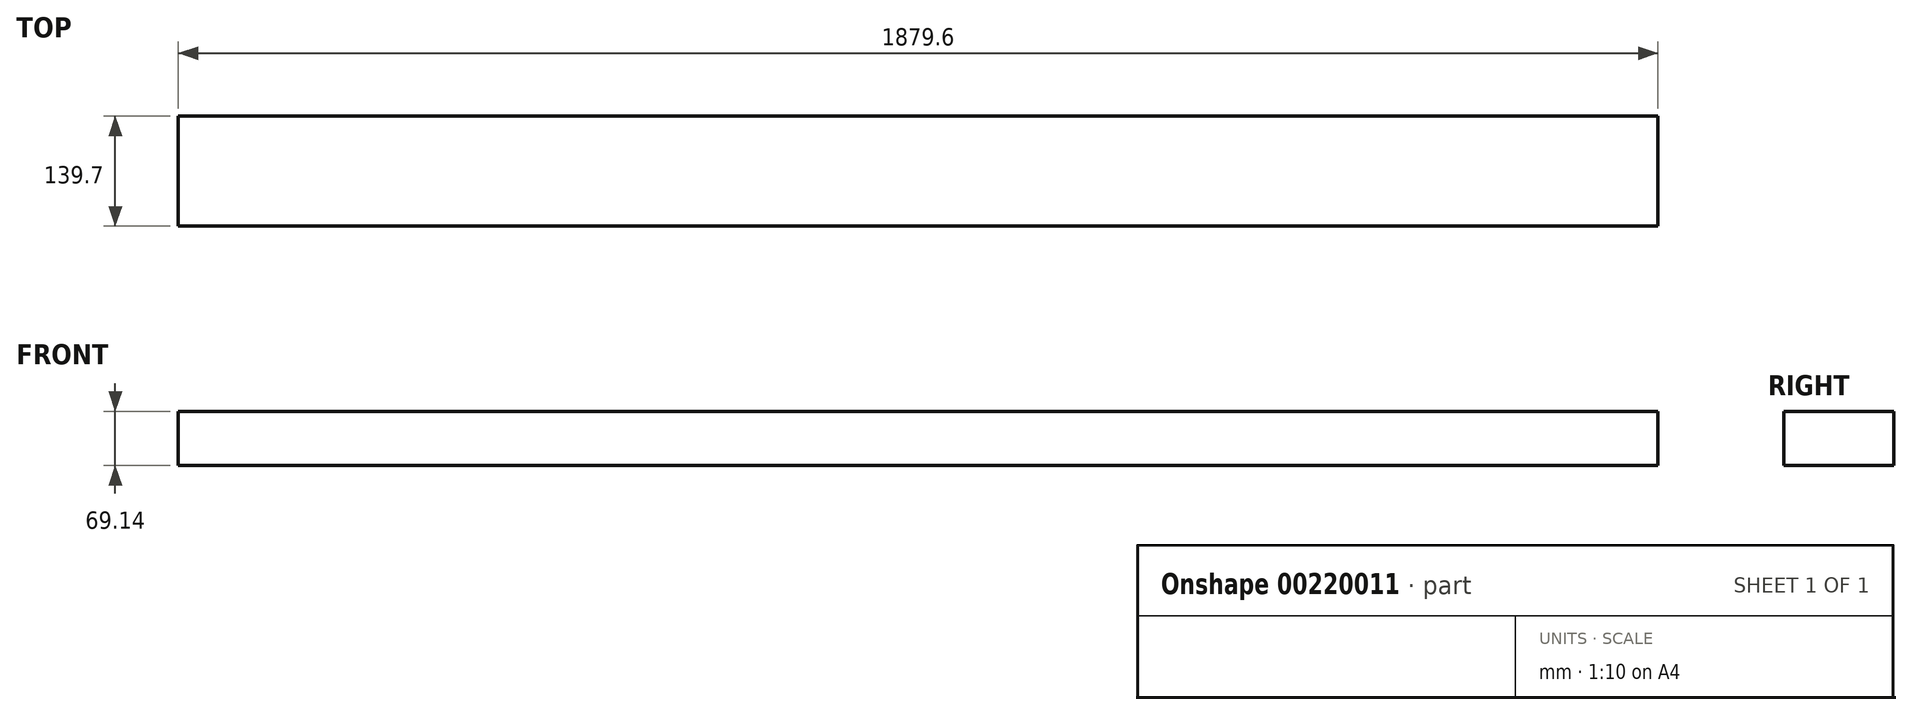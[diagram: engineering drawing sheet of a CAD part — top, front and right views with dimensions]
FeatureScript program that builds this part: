
annotation { "Feature Type Name" : "Feature", "Feature Type Description" : "" }
export const myFeature = defineFeature(function(context is Context, id is Id, definition is map)
    precondition{}
    {
        {
            var Q0;
            Q0=qCreatedBy(makeId("Top.planeOp"),FACE);
            var sketch = newSketch(context, id + "F0", { "sketchPlane" : qUnion([Q0])});
            skLineSegment(sketch, "E0.bottom", {"start": v(0, 0) * mm, "end": v(1879.6, 0) * mm});
            skLineSegment(sketch, "E0.top", {"start": v(0, -139.7) * mm, "end": v(1879.6, -139.7) * mm});
            skLineSegment(sketch, "E0.left", {"start": v(0, 0) * mm, "end": v(0, -139.7) * mm});
            skLineSegment(sketch, "E0.right", {"start": v(1879.6, 0) * mm, "end": v(1879.6, -139.7) * mm});
            skSolve(sketch);
        }
        {
            var Q0;
            Q0=makeQuery(id+"F0.imprint","IMPRINT",FACE,{"disambiguationData":[TD([[makeQuery(id+"F0.imprint","IMPRINT",EDGE,{"derivedFrom":sQuery(id+"F0.wireOp",EDGE,"E0.bottom")}),-1.0]])]});
            extrude(context, id + "F1", {"entities" : qUnion([Q0]), "depth" : 69.14 * mm});
        }
    });
